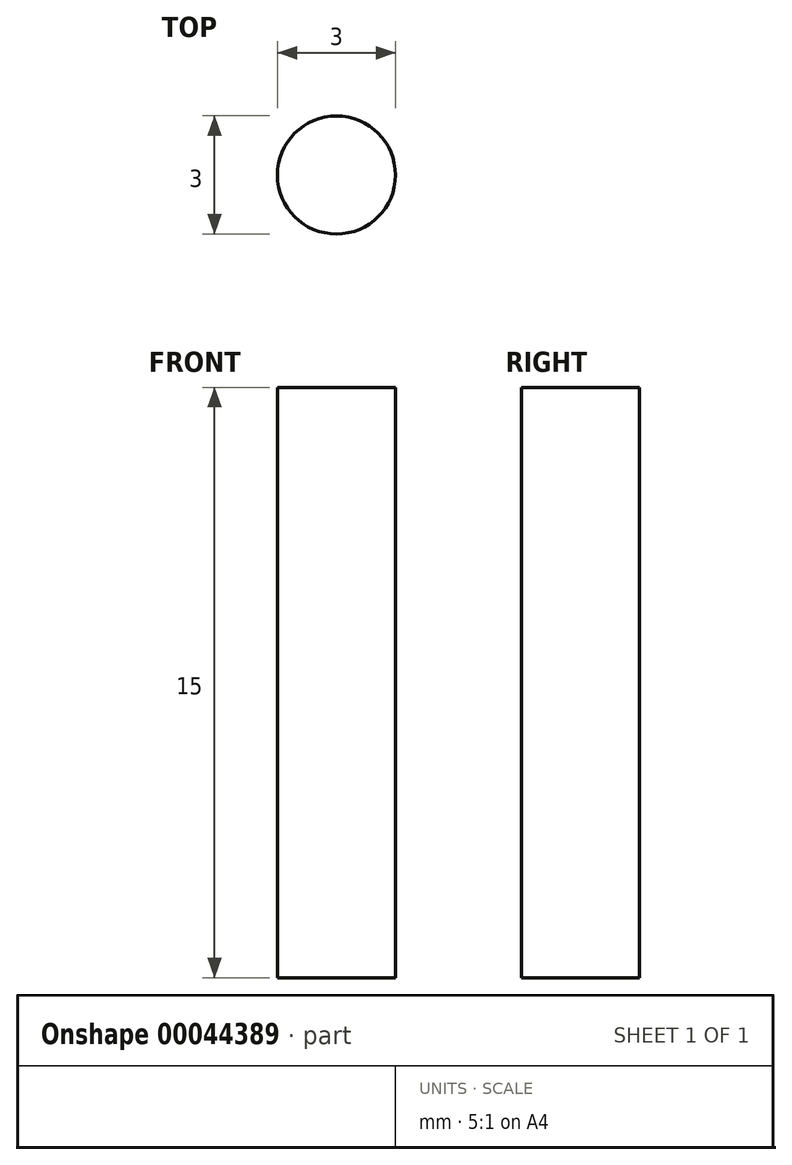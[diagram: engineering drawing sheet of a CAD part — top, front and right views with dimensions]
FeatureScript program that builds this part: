
annotation { "Feature Type Name" : "Feature", "Feature Type Description" : "" }
export const myFeature = defineFeature(function(context is Context, id is Id, definition is map)
    precondition{}
    {
        {
            var Q0;
            Q0=qCreatedBy(makeId("Top.planeOp"),FACE);
            var sketch = newSketch(context, id + "F0", { "sketchPlane" : qUnion([Q0])});
            skCircle(sketch, "E0", {"center": v(-80.28, 32.93) * mm, "radius": 1.5 * mm});
            skSolve(sketch);
        }
        {
            var Q0;
            Q0 = qSketchRegion(id + "F0", true);
            var Q1;
            Q1=makeQuery(id+"F0.imprint","IMPRINT",FACE,{"disambiguationData":[TD([[makeQuery(id+"F0.imprint","IMPRINT",EDGE,{"derivedFrom":sQuery(id+"F0.wireOp",EDGE,"E0")}),1.0]])]});
            extrude(context, id + "F1", {"entities" : qUnion([Q0, Q1]), "depth" : 15 * mm});
        }
    });
